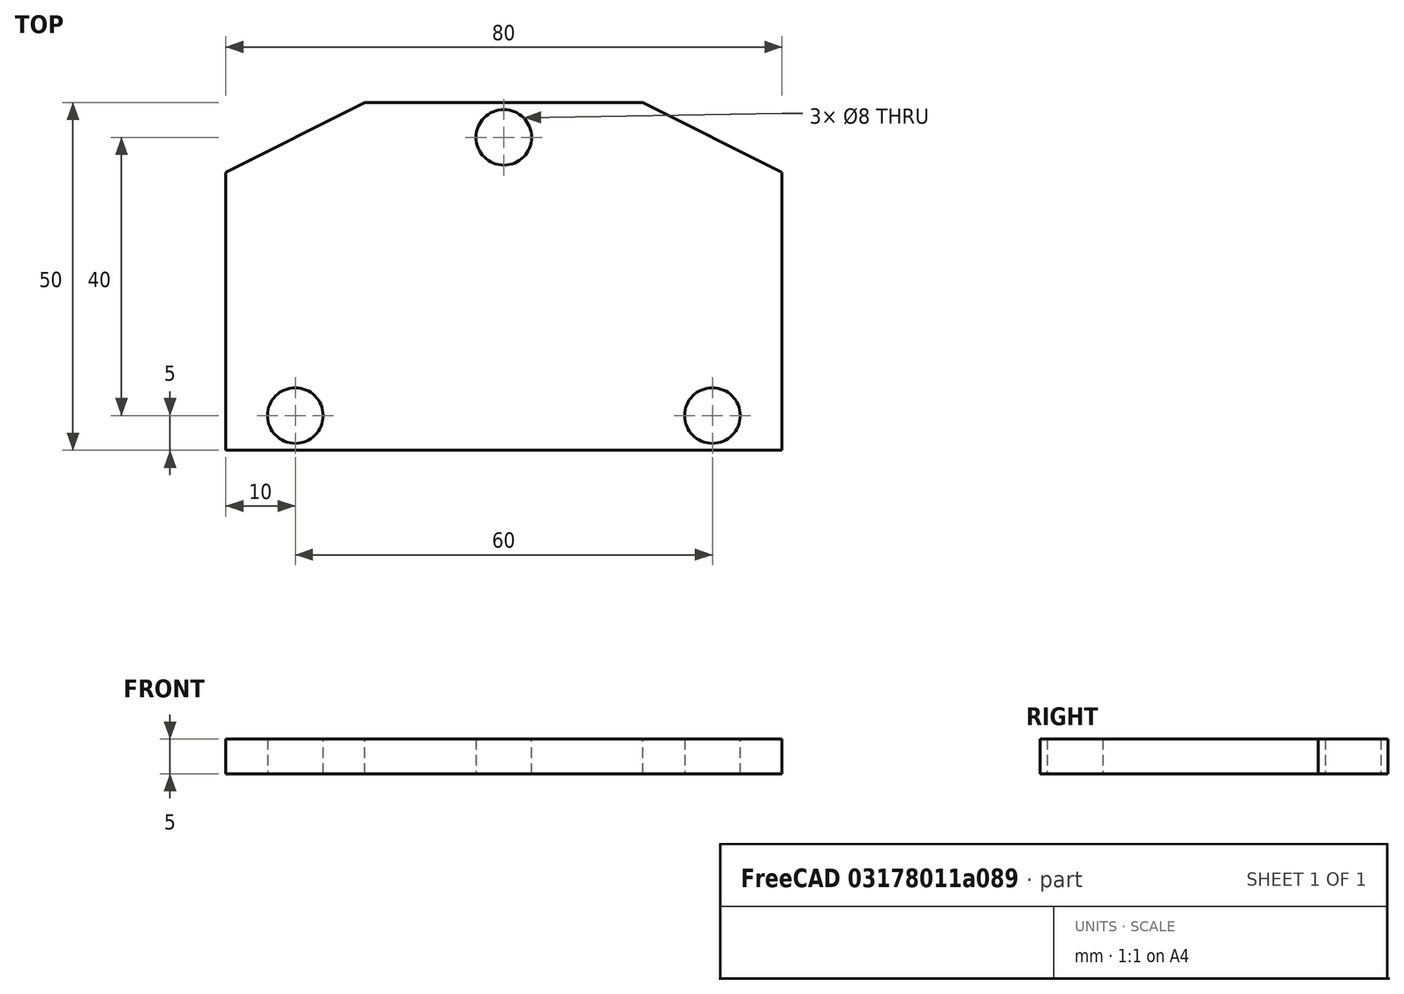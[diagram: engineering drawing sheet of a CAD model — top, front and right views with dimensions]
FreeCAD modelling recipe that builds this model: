
FCSTD DOCUMENT  (FreeCAD 0.16R6706 (Git))
Label: 20x20_linear_motion
License: All rights reserved
LicenseURL: http://en.wikipedia.org/wiki/All_rights_reserved
objects: Sketcher::SketchObject×1, PartDesign::Pad×1
note: 3 computed .brp shape members not serialized (recipe doc carries the construction recipe); baked Part::Feature solids carry a one-line shape summary decoded from their .brp

FEATURE [Sketcher::SketchObject] Sketch
  sketch-geometry (9):
    g0: LineSegment StartX=-20 StartY=20 StartZ=0 EndX=20 EndY=20 EndZ=0
    g1: LineSegment StartX=20 StartY=20 StartZ=0 EndX=40 EndY=10 EndZ=0
    g2: LineSegment StartX=40 StartY=10 StartZ=0 EndX=40 EndY=-30 EndZ=0
    g3: LineSegment StartX=40 StartY=-30 StartZ=0 EndX=-40 EndY=-30 EndZ=0
    g4: LineSegment StartX=-40 StartY=-30 StartZ=0 EndX=-40 EndY=10 EndZ=0
    g5: LineSegment StartX=-40 StartY=10 StartZ=0 EndX=-20 EndY=20 EndZ=0
    g6: Circle CenterX=-30 CenterY=-25 CenterZ=0 NormalX=0 NormalY=0 NormalZ=1 Radius=4
    g7: Circle CenterX=30 CenterY=-25 CenterZ=0 NormalX=0 NormalY=0 NormalZ=1 Radius=4
    g8: Circle CenterX=0 CenterY=15 CenterZ=0 NormalX=0 NormalY=0 NormalZ=1 Radius=4
  constraints (25):
    c: Coincident(g0,g1)
    c: Coincident(g1,g2)
    c: Coincident(g2,g3)
    c: Coincident(g3,g4)
    c: Coincident(g4,g5)
    c: Coincident(g5,g0)
    c: Horizontal(g3)
    c: Horizontal(g0)
    c: Vertical(g4)
    c: Vertical(g2)
    c: Symmetric(g0,g0,g-2)
    c: Symmetric(g4,g1,g-2)
    c: DistanceX(g-1,g0) = 20
    c: DistanceX(g-1,g1) = 40
    c: DistanceY(g-1,g1) = 10
    c: DistanceY(g-1,g0) = 20
    c: DistanceY(g2) = -30
    c: Radius(g8) = 4
    c: Radius(g6) = 4
    c: Radius(g7) = 4
    c: Symmetric(g6,g7,g-2)
    c: DistanceX(g-1,g7) = 30
    c: DistanceY(g7,g-1) = 25
    c: DistanceX(g8,g-1) = 0
    c: DistanceY(g-1,g8) = 15
FEATURE [PartDesign::Pad] Pad
  Length = 5
  Length2 = 100
  Sketch = -> Sketch
  Type = 0
